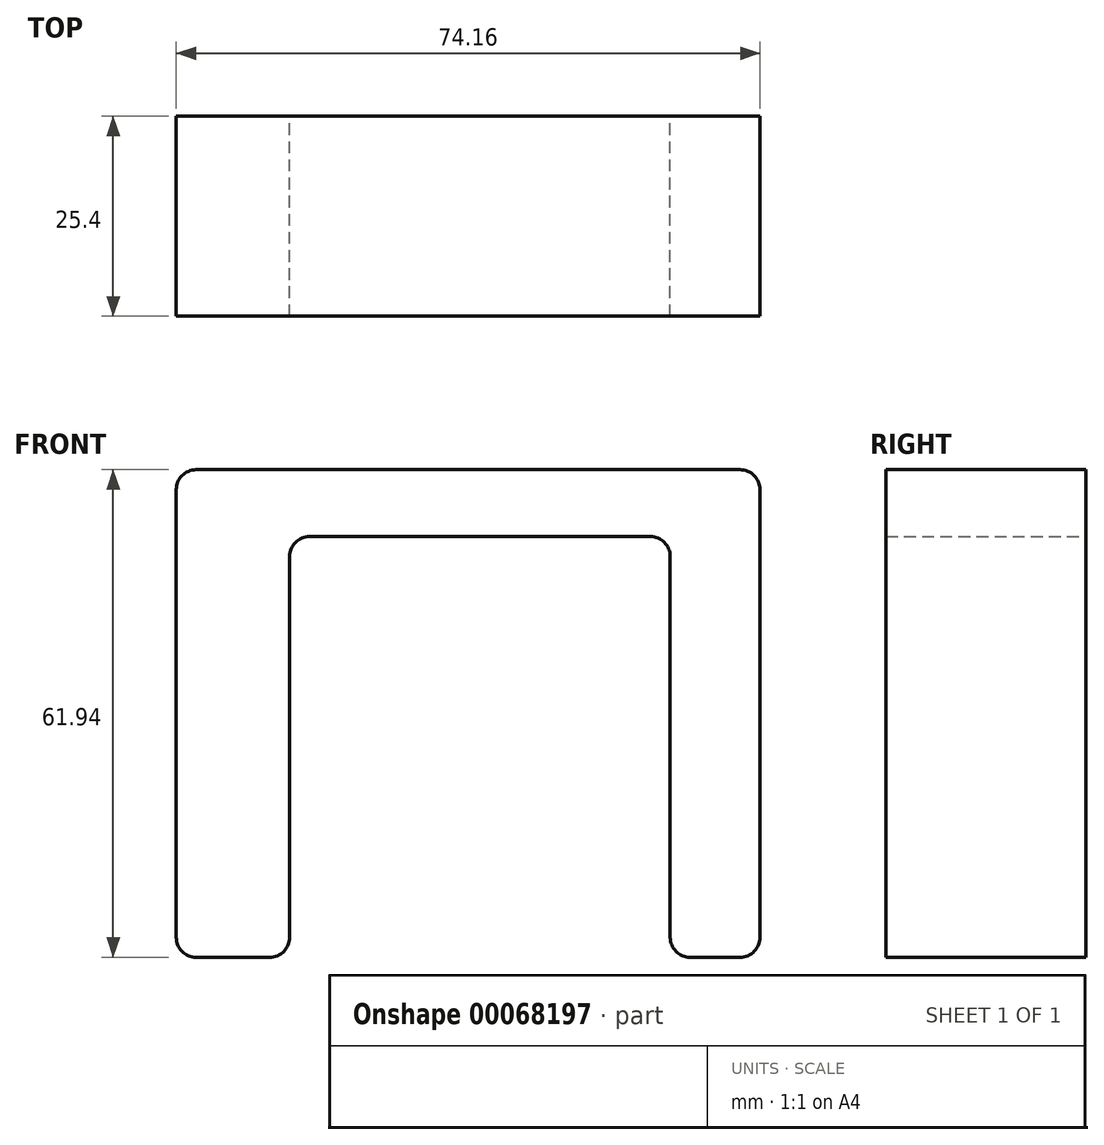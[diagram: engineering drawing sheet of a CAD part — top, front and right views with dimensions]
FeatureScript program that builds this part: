
annotation { "Feature Type Name" : "Feature", "Feature Type Description" : "" }
export const myFeature = defineFeature(function(context is Context, id is Id, definition is map)
    precondition{}
    {
        {
            var Q0;
            Q0=qCreatedBy(makeId("Front.planeOp"),FACE);
            var sketch = newSketch(context, id + "F0", { "sketchPlane" : qUnion([Q0])});
            skLineSegment(sketch, "E0.bottom", {"start": v(-32.89, 29.97) * mm, "end": v(36.19, 29.97) * mm});
            skLineSegment(sketch, "E0.top", {"start": v(-32.89, -31.97) * mm, "end": v(-23.56, -31.97) * mm});
            skLineSegment(sketch, "E0.left", {"start": v(-35.43, 27.43) * mm, "end": v(-35.43, -29.43) * mm});
            skLineSegment(sketch, "E0.right", {"start": v(38.73, 27.43) * mm, "end": v(38.73, -29.43) * mm});
            skLineSegment(sketch, "E1.bottom", {"start": v(-18.48, 21.47) * mm, "end": v(24.78, 21.47) * mm});
            skLineSegment(sketch, "E1.left", {"start": v(-21.02, 18.93) * mm, "end": v(-21.02, -29.43) * mm});
            skLineSegment(sketch, "E1.right", {"start": v(27.32, 18.93) * mm, "end": v(27.32, -29.43) * mm});
            skLineSegment(sketch, "E2.trimOffspring", {"start": v(29.86, -31.97) * mm, "end": v(36.19, -31.97) * mm});
            skPoint(sketch, "E3.visualSharp", {"position": v(-35.43, 29.97) * mm});
            skArc(sketch, "E3.filletArc", {"start": v(-32.89, 29.97) * mm, "mid": v(-34.68, 29.22) * mm, "end": v(-35.43, 27.43) * mm});
            skPoint(sketch, "E4.visualSharp", {"position": v(-21.02, 21.47) * mm});
            skArc(sketch, "E4.filletArc", {"start": v(-18.48, 21.47) * mm, "mid": v(-20.27, 20.72) * mm, "end": v(-21.02, 18.93) * mm});
            skPoint(sketch, "E5.visualSharp", {"position": v(38.73, 29.97) * mm});
            skArc(sketch, "E5.filletArc", {"start": v(38.73, 27.43) * mm, "mid": v(37.99, 29.22) * mm, "end": v(36.19, 29.97) * mm});
            skPoint(sketch, "E6.visualSharp", {"position": v(27.32, 21.47) * mm});
            skArc(sketch, "E6.filletArc", {"start": v(27.32, 18.93) * mm, "mid": v(26.58, 20.72) * mm, "end": v(24.78, 21.47) * mm});
            skPoint(sketch, "E7.visualSharp", {"position": v(-21.02, -31.97) * mm});
            skArc(sketch, "E7.filletArc", {"start": v(-23.56, -31.97) * mm, "mid": v(-21.76, -31.23) * mm, "end": v(-21.02, -29.43) * mm});
            skPoint(sketch, "E8.visualSharp", {"position": v(-35.43, -31.97) * mm});
            skArc(sketch, "E8.filletArc", {"start": v(-35.43, -29.43) * mm, "mid": v(-34.68, -31.23) * mm, "end": v(-32.89, -31.97) * mm});
            skPoint(sketch, "E9.visualSharp", {"position": v(38.73, -31.97) * mm});
            skArc(sketch, "E9.filletArc", {"start": v(36.19, -31.97) * mm, "mid": v(37.99, -31.23) * mm, "end": v(38.73, -29.43) * mm});
            skPoint(sketch, "E10.visualSharp", {"position": v(27.32, -31.97) * mm});
            skArc(sketch, "E10.filletArc", {"start": v(27.32, -29.43) * mm, "mid": v(28.06, -31.23) * mm, "end": v(29.86, -31.97) * mm});
            skSolve(sketch);
        }
        {
            var Q0;
            Q0=makeQuery(id+"F0.imprint","IMPRINT",FACE,{"disambiguationData":[TD([[makeQuery(id+"F0.imprint","IMPRINT",EDGE,{"derivedFrom":sQuery(id+"F0.wireOp",EDGE,"E0.bottom")}),-1.0]])]});
            extrude(context, id + "F1", {"entities" : qUnion([Q0]), "depth" : 25.4 * mm});
        }
    });
